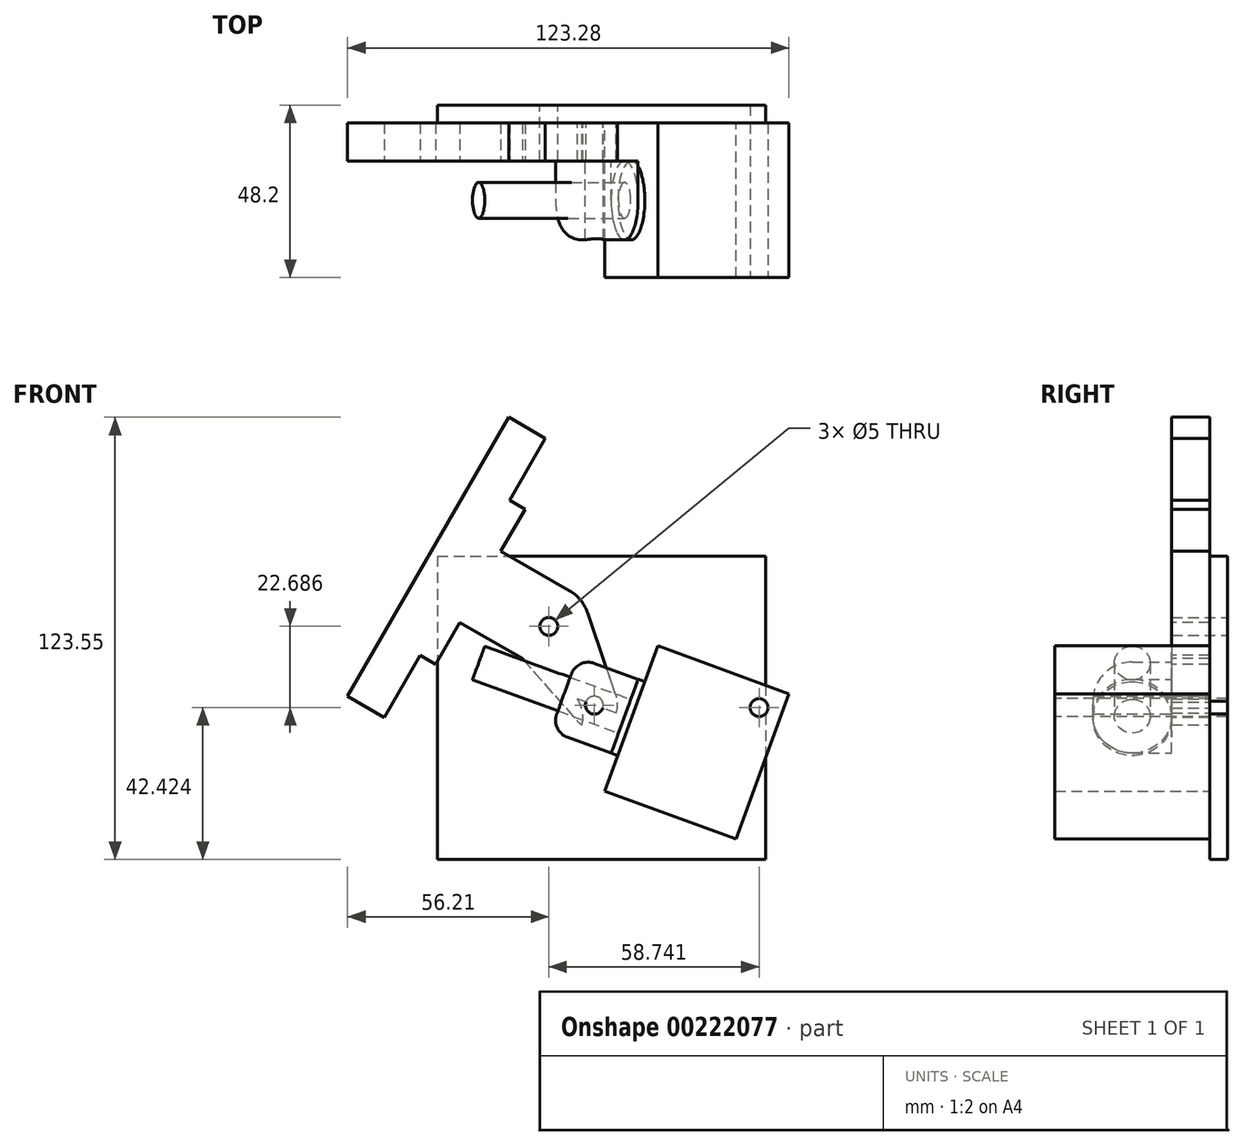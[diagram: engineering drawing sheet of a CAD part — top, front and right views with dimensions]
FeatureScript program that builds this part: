
annotation { "Feature Type Name" : "Feature", "Feature Type Description" : "" }
export const myFeature = defineFeature(function(context is Context, id is Id, definition is map)
    precondition{}
    {
        {
            var Q0;
            Q0=qCreatedBy(makeId("Front.planeOp"),FACE);
            var sketch = newSketch(context, id + "F0", { "sketchPlane" : qUnion([Q0])});
            skArc(sketch, "E0", {"start": v(10.9, 3.68) * mm, "mid": v(-5.75, 9.96) * mm, "end": v(-8.63, -7.6) * mm});
            skCircle(sketch, "E1", {"center": v(0, 0) * mm, "radius": 2.5 * mm});
            skLineSegment(sketch, "E2", {"start": v(-23.42, 12.9) * mm, "end": v(20.76, 12.9) * mm, "construction": true});
            skCircle(sketch, "E3", {"center": v(0, 0) * mm, "radius": 25.4 * mm, "construction": true});
            skLineSegment(sketch, "E4", {"start": v(0, 0) * mm, "end": v(12.7, -22) * mm, "construction": true});
            skLineSegment(sketch, "E5", {"start": v(12.7, -22) * mm, "end": v(23.04, -25.76) * mm, "construction": true});
            skLineSegment(sketch, "E6", {"start": v(23.04, -25.76) * mm, "end": v(26.8, -15.42) * mm, "construction": true});
            skLineSegment(sketch, "E7", {"start": v(19.27, -36.1) * mm, "end": v(23.04, -25.76) * mm, "construction": true});
            skLineSegment(sketch, "E8", {"start": v(23.04, -25.76) * mm, "end": v(30.42, -5.46) * mm});
            skLineSegment(sketch, "E9", {"start": v(23.04, -25.76) * mm, "end": v(15.65, -46.06) * mm});
            skLineSegment(sketch, "E10", {"start": v(15.65, -46.06) * mm, "end": v(52.3, -59.4) * mm});
            skLineSegment(sketch, "E11", {"start": v(30.42, -5.46) * mm, "end": v(67.07, -18.8) * mm});
            skLineSegment(sketch, "E12", {"start": v(67.07, -18.8) * mm, "end": v(52.3, -59.4) * mm});
            skArc(sketch, "E13", {"start": v(7.82, -26.3) * mm, "mid": v(15.95, -27.63) * mm, "end": v(18.86, -19.92) * mm});
            skLineSegment(sketch, "E14", {"start": v(-8.63, -7.6) * mm, "end": v(7.82, -26.3) * mm});
            skLineSegment(sketch, "E15", {"start": v(10.9, 3.68) * mm, "end": v(18.86, -19.92) * mm});
            skCircle(sketch, "E16", {"center": v(12.7, -22) * mm, "radius": 2.5 * mm});
            skCircle(sketch, "E17", {"center": v(-23.87, -8.69) * mm, "radius": 6.5 * mm});
            skPoint(sketch, "E18.startSnap0", {"position": v(-8.16, -9.73) * mm});
            skLineSegment(sketch, "E19", {"start": v(-15.41, -11.77) * mm, "end": v(-19.17, -22.1) * mm});
            skLineSegment(sketch, "E20", {"start": v(-19.17, -22.1) * mm, "end": v(-11.65, -1.43) * mm});
            skLineSegment(sketch, "E21", {"start": v(-11.65, -1.43) * mm, "end": v(-23.86, 3.02) * mm});
            skLineSegment(sketch, "E22", {"start": v(-30.27, 0.03) * mm, "end": v(-34.38, -11.25) * mm});
            skLineSegment(sketch, "E23", {"start": v(-31.39, -17.66) * mm, "end": v(-19.17, -22.1) * mm});
            skPoint(sketch, "E24.visualSharp", {"position": v(-28.56, 4.73) * mm});
            skArc(sketch, "E24.filletArc", {"start": v(-23.86, 3.02) * mm, "mid": v(-27.69, 2.85) * mm, "end": v(-30.27, 0.03) * mm});
            skPoint(sketch, "E25.visualSharp", {"position": v(-36.09, -15.95) * mm});
            skArc(sketch, "E25.filletArc", {"start": v(-34.38, -11.25) * mm, "mid": v(-34.21, -15.07) * mm, "end": v(-31.39, -17.66) * mm});
            skLineSegment(sketch, "E26", {"start": v(-27.76, 12.9) * mm, "end": v(-49.26, -46.16) * mm, "construction": true});
            skLineSegment(sketch, "E27", {"start": v(23.04, -25.76) * mm, "end": v(-23.87, -8.69) * mm});
            skLineSegment(sketch, "E28", {"start": v(-23.87, -8.69) * mm, "end": v(0, 0) * mm, "construction": true});
            skLineSegment(sketch, "E29", {"start": v(18.09, 12.9) * mm, "end": v(75.65, -20.33) * mm, "construction": true});
            skLineSegment(sketch, "E30", {"start": v(12.82, -40.87) * mm, "end": v(-42.18, -40.87) * mm});
            skLineSegment(sketch, "E31", {"start": v(-42.18, -40.87) * mm, "end": v(-42.18, -56.87) * mm});
            skLineSegment(sketch, "E32", {"start": v(-42.18, -56.87) * mm, "end": v(12.82, -56.87) * mm});
            skLineSegment(sketch, "E33", {"start": v(12.82, -56.87) * mm, "end": v(12.82, -40.87) * mm});
            skCircle(sketch, "E34", {"center": v(0, -25.4) * mm, "radius": 9.5 * mm});
            skLineSegment(sketch, "E35", {"start": v(0, 0) * mm, "end": v(-32.89, 11.97) * mm});
            skLineSegment(sketch, "E36", {"start": v(-32.89, 11.97) * mm, "end": v(-48.28, -30.32) * mm});
            skLineSegment(sketch, "E37", {"start": v(-32.89, 11.97) * mm, "end": v(-31.18, 16.67) * mm});
            skLineSegment(sketch, "E38", {"start": v(-31.18, 16.67) * mm, "end": v(-42.46, 20.77) * mm});
            skLineSegment(sketch, "E39", {"start": v(-42.46, 20.77) * mm, "end": v(-59.56, -26.21) * mm});
            skLineSegment(sketch, "E40", {"start": v(-48.28, -30.32) * mm, "end": v(-59.56, -26.21) * mm});
            skLineSegment(sketch, "E41", {"start": v(-14.68, -40.87) * mm, "end": v(-14.68, -91.76) * mm});
            skSolve(sketch);
        }
        {
            var Q0;
            Q0=makeQuery(id+"F0.imprint","IMPRINT",FACE,{"disambiguationData":[TD([[makeQuery(id+"F0.imprint","IMPRINT",EDGE,{"derivedFrom":sQuery(id+"F0.wireOp",EDGE,"E0")}),1.0]])]});
            var Q1;
            {var subQ0=sQuery(id+"F0.wireOp",EDGE,"E21");var subQ1=sQuery(id+"F0.wireOp",EDGE,"E14");var subQ2=makeQuery(id+"F0.imprint","INTERSECT",VERTEX,{"derivedFrom":[subQ1,subQ0]});Q1=makeQuery(id+"F0.imprint","IMPRINT",FACE,{"disambiguationData":[TD([[makeQuery(id+"F0.imprint","IMPRINT",EDGE,{"disambiguationData":[TD([[subQ2,-1.0]])],"derivedFrom":subQ1}),1.0]])]});}
            var Q2;
            {var subQ1=sQuery(id+"F0.wireOp",EDGE,"E13");var subQ6=sQuery(id+"F0.wireOp",EDGE,"E14");var subQ7=makeQuery(id+"F0.imprint","INTERSECT",VERTEX,{"derivedFrom":[subQ1,subQ6]});Q2=makeQuery(id+"F0.imprint","IMPRINT",FACE,{"disambiguationData":[TD([[makeQuery(id+"F0.imprint","IMPRINT",EDGE,{"disambiguationData":[TD([[subQ7,-1.0]])],"derivedFrom":subQ1}),1.0]])]});}
            extrude(context, id + "F1", {"entities" : qUnion([Q0, Q1, Q2]), "depth" : 10.6 * mm, "offsetDistance" : 25 * mm});
        }
        {
            var Q0;
            Q0=makeQuery(id+"F0.imprint","IMPRINT",FACE,{"disambiguationData":[TD([[makeQuery(id+"F0.imprint","IMPRINT",EDGE,{"derivedFrom":sQuery(id+"F0.wireOp",EDGE,"E8")}),-1.0]])]});
            extrude(context, id + "F2", {"entities" : qUnion([Q0]), "depth" : 43.2 * mm, "offsetDistance" : 25 * mm});
        }
        {
            var Q0;
            Q0=makeQuery(id+"F2.opExtrude","SWEPT_FACE",FACE,{"disambiguationData":[OSD([sQuery(id+"F0.wireOp",EDGE,"E8"),sQuery(id+"F0.wireOp",EDGE,"E9")])]});
            var sketch = newSketch(context, id + "F3", { "sketchPlane" : qUnion([Q0])});
            skCircle(sketch, "E42", {"center": v(21.6, -16.33) * mm, "radius": 11 * mm});
            skPoint(sketch, "E42.centerSnap0", {"position": v(43.2, -16.33) * mm});
            skPoint(sketch, "E42.centerSnap1", {"position": v(21.6, 5.27) * mm});
            skSolve(sketch);
        }
        {
            var Q0;
            Q0=makeQuery(id+"F3.imprint","IMPRINT",FACE,{"disambiguationData":[TD([[makeQuery(id+"F3.imprint","IMPRINT",EDGE,{"derivedFrom":sQuery(id+"F3.wireOp",EDGE,"E42")}),1.0]])]});
            extrude(context, id + "F4", {"entities" : qUnion([Q0]), "operationType" : NewBodyOperationType.ADD, "depth" : 2 * mm, "offsetDistance" : 25 * mm});
        }
        {
            var Q0;
            Q0=makeQuery(id+"F4.opExtrude","CAP_FACE",FACE,{"disambiguationData":[OSD([sQuery(id+"F3.wireOp",EDGE,"E42")])],"isStart":false});
            var sketch = newSketch(context, id + "F5", { "sketchPlane" : qUnion([Q0])});
            skCircle(sketch, "E43.0", {"center": v(21.6, -16.33) * mm, "radius": 11 * mm});
            skCircle(sketch, "E44", {"center": v(21.6, -16.33) * mm, "radius": 5 * mm});
            skSolve(sketch);
        }
        {
            var Q0;
            Q0=makeQuery(id+"F5.imprint","IMPRINT",FACE,{"disambiguationData":[TD([[makeQuery(id+"F5.imprint","IMPRINT",EDGE,{"derivedFrom":sQuery(id+"F5.wireOp",EDGE,"E44")}),1.0]])]});
            extrude(context, id + "F6", {"entities" : qUnion([Q0]), "operationType" : NewBodyOperationType.ADD, "depth" : (45.4 - 2) * mm, "offsetDistance" : 25 * mm});
        }
        {
            var Q0;
            Q0=makeQuery(id+"F1.opExtrude","CAP_FACE",FACE,{"disambiguationData":[OSD([sQuery(id+"F0.wireOp",EDGE,"E0"),sQuery(id+"F0.wireOp",EDGE,"E1"),sQuery(id+"F0.wireOp",EDGE,"E13"),sQuery(id+"F0.wireOp",EDGE,"E14"),sQuery(id+"F0.wireOp",EDGE,"E15"),sQuery(id+"F0.wireOp",EDGE,"E16")])],"isStart":false});
            var sketch = newSketch(context, id + "F7", { "sketchPlane" : qUnion([Q0])});
            skCircle(sketch, "E45.0", {"center": v(12.7, -22) * mm, "radius": 2.5 * mm});
            skLineSegment(sketch, "E46.0", {"start": v(17.4, -35.41) * mm, "end": v(24.92, -14.74) * mm});
            skLineSegment(sketch, "E47", {"start": v(24.92, -14.74) * mm, "end": v(8, -8.58) * mm});
            skLineSegment(sketch, "E48", {"start": v(17.4, -35.41) * mm, "end": v(0.48, -29.26) * mm});
            skLineSegment(sketch, "E49", {"start": v(8, -8.58) * mm, "end": v(0.48, -29.26) * mm});
            skSolve(sketch);
        }
        {
            var Q0;
            {var subQ1=sQuery(id+"F7.wireOp",EDGE,"E48");Q0=makeQuery(id+"F7.imprint","IMPRINT",FACE,{"disambiguationData":[TD([[makeQuery(id+"F7.imprint","IMPRINT",EDGE,{"derivedFrom":subQ1}),-1.0]])]});}
            var Q1;
            Q1=makeQuery(id+"F7.imprint","IMPRINT",FACE,{"disambiguationData":[TD([[makeQuery(id+"F7.imprint","IMPRINT",EDGE,{"derivedFrom":sQuery(id+"F7.wireOp",EDGE,"E45.0")}),-1.0]])]});
            var Q2;
            {var subQ0=sQuery(id+"F7.wireOp",EDGE,"E47");var subQ1=sQuery(id+"F7.wireOp",EDGE,"E46.0");var subQ2=makeQuery(id+"F7.imprint","INTERSECT",VERTEX,{"derivedFrom":[subQ1,subQ0]});Q2=makeQuery(id+"F7.imprint","IMPRINT",FACE,{"disambiguationData":[TD([[makeQuery(id+"F7.imprint","IMPRINT",EDGE,{"disambiguationData":[TD([[subQ2,1.0]])],"derivedFrom":subQ1}),1.0]])]});}
            var Q3;
            {var subQ8=sQuery(id+"F0.wireOp",EDGE,"E13");var subQ9=makeQuery(id+"F1.opExtrude","CAP_EDGE",EDGE,{"disambiguationData":[OSD([subQ8])],"isStart":false});Q3=makeQuery(id+"F7.imprint","IMPRINT",FACE,{"disambiguationData":[TD([[makeQuery(id+"F7.imprint","IMPRINT",EDGE,{"derivedFrom":subQ9}),1.0]])]});}
            extrude(context, id + "F8", {"entities" : qUnion([Q0, Q1, Q2, Q3]), "depth" : 22 * mm, "offsetDistance" : 25 * mm});
        }
        {
            var Q0;
            Q0=makeQuery(id+"F8.opExtrude","CAP_EDGE",EDGE,{"disambiguationData":[OSD([sQuery(id+"F7.wireOp",EDGE,"E47")])],"isStart":false});
            var Q1;
            Q1=makeQuery(id+"F8.opExtrude","CAP_EDGE",EDGE,{"disambiguationData":[OSD([sQuery(id+"F7.wireOp",EDGE,"E48")])],"isStart":false});
            fillet(context, id + "F9", {"entities" : qUnion([Q0, Q1]), "radius" : 11 * mm, "tangentPropagation" : true, "allowEdgeOverflow" : false});
        }
        {
            var Q0;
            Q0=makeQuery(id+"F0.imprint","IMPRINT",FACE,{"disambiguationData":[TD([[makeQuery(id+"F0.imprint","IMPRINT",EDGE,{"derivedFrom":sQuery(id+"F0.wireOp",EDGE,"E0")}),1.0]])]});
            var sketch = newSketch(context, id + "F10", { "sketchPlane" : qUnion([Q0])});
            skLineSegment(sketch, "E50.bottom", {"start": v(-31.15, 19.66) * mm, "end": v(60.52, 19.66) * mm});
            skLineSegment(sketch, "E50.top", {"start": v(-31.15, -65.11) * mm, "end": v(60.52, -65.11) * mm});
            skLineSegment(sketch, "E50.left", {"start": v(-31.15, 19.66) * mm, "end": v(-31.15, -65.11) * mm});
            skLineSegment(sketch, "E50.right", {"start": v(60.52, 19.66) * mm, "end": v(60.52, -65.11) * mm});
            skSolve(sketch);
        }
        {
            var Q0;
            Q0=makeQuery(id+"F10.imprint","IMPRINT",FACE,{"disambiguationData":[TD([[makeQuery(id+"F10.imprint","IMPRINT",EDGE,{"derivedFrom":sQuery(id+"F10.wireOp",EDGE,"E50.bottom")}),-1.0]])]});
            var Q1;
            Q1=makeQuery(id+"F0.imprint","IMPRINT",FACE,{"disambiguationData":[TD([[makeQuery(id+"F0.imprint","IMPRINT",EDGE,{"derivedFrom":sQuery(id+"F0.wireOp",EDGE,"E0")}),1.0]])]});
            var Q2;
            Q2=makeQuery(id+"F0.imprint","IMPRINT",FACE,{"disambiguationData":[TD([[makeQuery(id+"F0.imprint","IMPRINT",EDGE,{"derivedFrom":sQuery(id+"F0.wireOp",EDGE,"E16")}),1.0]])]});
            extrude(context, id + "F11", {"entities" : qUnion([Q0, Q1, Q2]), "oppositeDirection" : true, "depth" : 5 * mm, "offsetDistance" : 25 * mm});
        }
        {
            var Q0;
            Q0=makeQuery(id+"F2.opExtrude","CAP_FACE",FACE,{"disambiguationData":[OSD([sQuery(id+"F0.wireOp",EDGE,"E8"),sQuery(id+"F0.wireOp",EDGE,"E9"),sQuery(id+"F0.wireOp",EDGE,"E10"),sQuery(id+"F0.wireOp",EDGE,"E11"),sQuery(id+"F0.wireOp",EDGE,"E12")])],"isStart":false});
            var sketch = newSketch(context, id + "F12", { "sketchPlane" : qUnion([Q0])});
            skCircle(sketch, "E51", {"center": v(58.74, -22.69) * mm, "radius": 6.5 * mm});
            skCircle(sketch, "E52", {"center": v(58.74, -22.69) * mm, "radius": 2.5 * mm});
            skSolve(sketch);
        }
        {
            var Q0;
            Q0=makeQuery(id+"F12.imprint","IMPRINT",FACE,{"disambiguationData":[TD([[makeQuery(id+"F12.imprint","IMPRINT",EDGE,{"derivedFrom":sQuery(id+"F12.wireOp",EDGE,"E52")}),1.0]])]});
            extrude(context, id + "F13", {"entities" : qUnion([Q0]), "operationType" : NewBodyOperationType.REMOVE, "oppositeDirection" : true, "depth" : 74.8 * mm, "offsetDistance" : 25 * mm});
        }
        {
            var Q0;
            Q0=makeQuery(id+"F1.opExtrude","CAP_FACE",FACE,{"disambiguationData":[OSD([sQuery(id+"F0.wireOp",EDGE,"E0"),sQuery(id+"F0.wireOp",EDGE,"E1"),sQuery(id+"F0.wireOp",EDGE,"E13"),sQuery(id+"F0.wireOp",EDGE,"E14"),sQuery(id+"F0.wireOp",EDGE,"E15"),sQuery(id+"F0.wireOp",EDGE,"E16")])],"isStart":false});
            var sketch = newSketch(context, id + "F14", { "sketchPlane" : qUnion([Q0])});
            skLineSegment(sketch, "E53", {"start": v(-24.91, 1.1) * mm, "end": v(-31.66, -10.59) * mm});
            skLineSegment(sketch, "E54", {"start": v(-31.66, -10.59) * mm, "end": v(-36, -8.09) * mm});
            skLineSegment(sketch, "E55", {"start": v(-36, -8.09) * mm, "end": v(-17.74, 23.52) * mm});
            skLineSegment(sketch, "E56", {"start": v(-13.41, 21.02) * mm, "end": v(5.75, 9.96) * mm});
            skArc(sketch, "E57.0", {"start": v(10.9, 3.68) * mm, "mid": v(-5.75, 9.96) * mm, "end": v(-8.63, -7.6) * mm});
            skLineSegment(sketch, "E58", {"start": v(-24.91, 1.1) * mm, "end": v(-7.39, -9.02) * mm});
            skLineSegment(sketch, "E59.0", {"start": v(-21.34, -14.93) * mm, "end": v(-17.92, -5.53) * mm});
            skLineSegment(sketch, "E60", {"start": v(-13.41, 21.02) * mm, "end": v(-6.66, 32.72) * mm});
            skLineSegment(sketch, "E61", {"start": v(-17.74, 23.52) * mm, "end": v(-11, 35.22) * mm});
            skLineSegment(sketch, "E62", {"start": v(-11, 35.22) * mm, "end": v(-6.66, 32.72) * mm});
            skLineSegment(sketch, "E63", {"start": v(-1, 52.54) * mm, "end": v(-46, -25.4) * mm});
            skLineSegment(sketch, "E64", {"start": v(-46, -25.4) * mm, "end": v(-56.21, -19.5) * mm});
            skLineSegment(sketch, "E65", {"start": v(-56.21, -19.5) * mm, "end": v(-11.21, 58.44) * mm});
            skLineSegment(sketch, "E66", {"start": v(-1, 52.54) * mm, "end": v(-11.21, 58.44) * mm});
            skLineSegment(sketch, "E67", {"start": v(0, 0) * mm, "end": v(-23.5, 13.56) * mm});
            skLineSegment(sketch, "E68", {"start": v(-36, -8.09) * mm, "end": v(-41.62, -4.84) * mm});
            skLineSegment(sketch, "E69", {"start": v(-41.62, -4.84) * mm, "end": v(-16.62, 38.47) * mm});
            skLineSegment(sketch, "E70", {"start": v(-11, 35.22) * mm, "end": v(-16.62, 38.47) * mm});
            skLineSegment(sketch, "E71.0", {"start": v(-8.63, -7.6) * mm, "end": v(-8.63, -7.6) * mm});
            skLineSegment(sketch, "E72.bottom", {"start": v(44.17, -61.4) * mm, "end": v(0.97, -61.4) * mm, "construction": true});
            skLineSegment(sketch, "E72.top", {"start": v(44.17, -8.4) * mm, "end": v(0.97, -8.4) * mm, "construction": true});
            skLineSegment(sketch, "E72.left", {"start": v(44.17, -61.4) * mm, "end": v(44.17, -8.4) * mm, "construction": true});
            skLineSegment(sketch, "E72.right", {"start": v(0.97, -61.4) * mm, "end": v(0.97, -8.4) * mm, "construction": true});
            skPoint(sketch, "E72.middle", {"position": v(22.57, -34.9) * mm});
            skLineSegment(sketch, "E73.bottom", {"start": v(61.57, -61.4) * mm, "end": v(-16.43, -61.4) * mm, "construction": true});
            skLineSegment(sketch, "E73.top", {"start": v(61.57, -79.4) * mm, "end": v(-16.43, -79.4) * mm, "construction": true});
            skLineSegment(sketch, "E73.left", {"start": v(61.57, -61.4) * mm, "end": v(61.57, -79.4) * mm, "construction": true});
            skLineSegment(sketch, "E73.right", {"start": v(-16.43, -61.4) * mm, "end": v(-16.43, -79.4) * mm, "construction": true});
            skPoint(sketch, "E73.middle", {"position": v(22.57, -70.4) * mm});
            skPoint(sketch, "E73.middle.positionSnap0", {"position": v(22.57, -61.4) * mm});
            skPoint(sketch, "E73.cornerSnap0", {"position": v(22.57, -61.4) * mm});
            skPoint(sketch, "E73.centerSnap0", {"position": v(22.57, -61.4) * mm});
            skCircle(sketch, "E74", {"center": v(0, 0) * mm, "radius": 24.94 * mm, "construction": true});
            skLineSegment(sketch, "E75", {"start": v(-26.34, -14.9) * mm, "end": v(-26.34, -49.9) * mm});
            skLineSegment(sketch, "E76", {"start": v(-24.94, 0) * mm, "end": v(-26.34, -14.9) * mm});
            skLineSegment(sketch, "E77.0", {"start": v(30.42, -5.46) * mm, "end": v(67.07, -18.8) * mm});
            skLineSegment(sketch, "E78", {"start": v(24.94, 0) * mm, "end": v(71.07, -16.8) * mm});
            skLineSegment(sketch, "E79", {"start": v(71.07, -16.8) * mm, "end": v(71.07, -49.9) * mm});
            skPoint(sketch, "E80.start.orphan", {"position": v(61.57, -56.36) * mm});
            skLineSegment(sketch, "E81.0", {"start": v(15.65, -46.06) * mm, "end": v(52.3, -59.4) * mm});
            skSolve(sketch);
        }
        {
            var Q0;
            Q0=makeQuery(id+"F14.imprint","IMPRINT",FACE,{"disambiguationData":[TD([[makeQuery(id+"F14.imprint","IMPRINT",EDGE,{"derivedFrom":sQuery(id+"F14.wireOp",EDGE,"E53")}),-1.0]])]});
            var Q1;
            {var subQ2=sQuery(id+"F14.wireOp",EDGE,"E56");Q1=makeQuery(id+"F14.imprint","IMPRINT",FACE,{"disambiguationData":[TD([[makeQuery(id+"F14.imprint","IMPRINT",EDGE,{"derivedFrom":subQ2}),-1.0]])]});}
            var Q2;
            {var subQ0=sQuery(id+"F14.wireOp",EDGE,"E68");Q2=makeQuery(id+"F14.imprint","IMPRINT",FACE,{"disambiguationData":[TD([[makeQuery(id+"F14.imprint","IMPRINT",EDGE,{"derivedFrom":subQ0}),-1.0]])]});}
            var Q3;
            {var subQ0=sQuery(id+"F14.wireOp",EDGE,"E64");Q3=makeQuery(id+"F14.imprint","IMPRINT",FACE,{"disambiguationData":[TD([[makeQuery(id+"F14.imprint","IMPRINT",EDGE,{"derivedFrom":subQ0}),-1.0]])]});}
            extrude(context, id + "F15", {"entities" : qUnion([Q0, Q1, Q2, Q3]), "operationType" : NewBodyOperationType.ADD, "oppositeDirection" : true, "depth" : 10.6 * mm, "offsetDistance" : 25 * mm});
        }
        {
            var Q0;
            Q0=makeQuery(id+"F9.opFillet","BLEND_EDGE",EDGE,{"blendedFrom":[makeQuery(id+"F8.opExtrude","CAP_EDGE",EDGE,{"disambiguationData":[OSD([sQuery(id+"F7.wireOp",EDGE,"E47")])],"isStart":false}),makeQuery(id+"F8.opExtrude","SWEPT_FACE",FACE,{"disambiguationData":[OSD([sQuery(id+"F7.wireOp",EDGE,"E49")])]})],"blendedInto":[makeQuery(id+"F8.opExtrude","SWEPT_FACE",FACE,{"disambiguationData":[OSD([sQuery(id+"F7.wireOp",EDGE,"E49")])]})]});
            fillet(context, id + "F16", {"entities" : qUnion([Q0]), "radius" : 5 * mm, "tangentPropagation" : true, "allowEdgeOverflow" : false});
        }
    });
